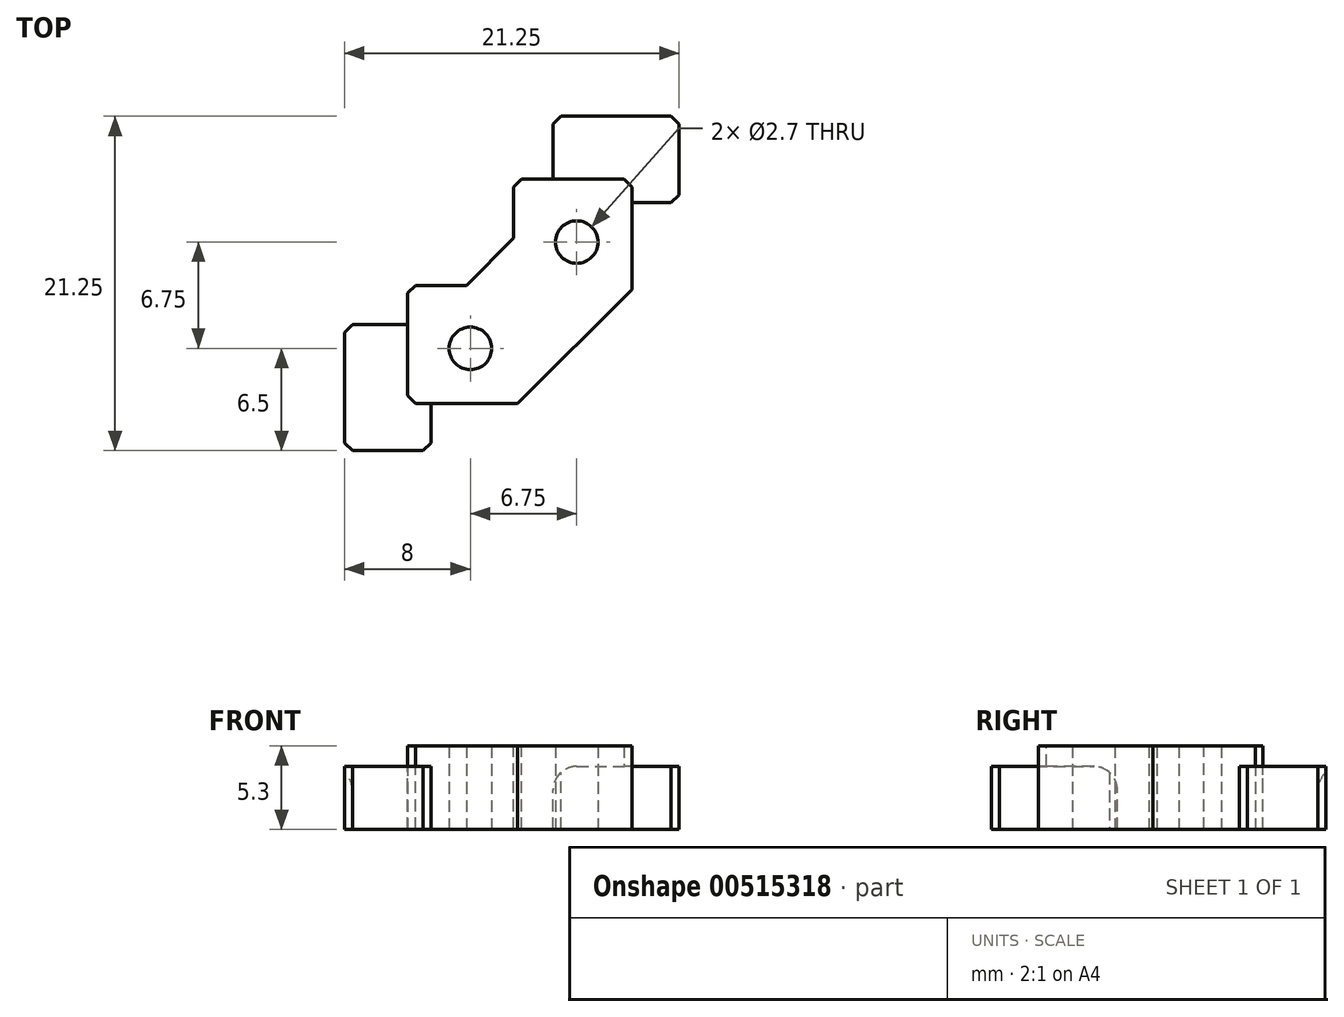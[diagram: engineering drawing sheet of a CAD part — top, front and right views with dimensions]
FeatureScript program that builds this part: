
annotation { "Feature Type Name" : "Feature", "Feature Type Description" : "" }
export const myFeature = defineFeature(function(context is Context, id is Id, definition is map)
    precondition{}
    {
        {
            var Q0;
            Q0=qCreatedBy(makeId("Top.planeOp"),FACE);
            var sketch = newSketch(context, id + "F0", { "sketchPlane" : qUnion([Q0])});
            skLineSegment(sketch, "E0", {"start": v(-0.25, -7) * mm, "end": v(7, 0.25) * mm});
            skLineSegment(sketch, "E1", {"start": v(7, 7.25) * mm, "end": v(7, 0.25) * mm});
            skLineSegment(sketch, "E2", {"start": v(-7.25, -7) * mm, "end": v(-0.25, -7) * mm});
            skLineSegment(sketch, "E3", {"start": v(-0.5, 7.25) * mm, "end": v(-0.5, 0.5) * mm});
            skLineSegment(sketch, "E4", {"start": v(-7.25, 0.5) * mm, "end": v(-0.5, 0.5) * mm});
            skLineSegment(sketch, "E5", {"start": v(-0.5, 7.25) * mm, "end": v(7, 7.25) * mm});
            skLineSegment(sketch, "E6", {"start": v(-7.25, 0.5) * mm, "end": v(-7.25, -7) * mm});
            skSolve(sketch);
        }
        {
            var Q0;
            Q0=qSketchRegion(id+"F0",true);
            extrude(context, id + "F1", {"entities" : qUnion([Q0]), "depth" : 1.3 * mm, "offsetDistance" : 25 * mm});
        }
        {
            var Q0;
            Q0=makeQuery(id+"F1.opExtrude","CAP_FACE",FACE,{"disambiguationData":[OSD([sQuery(id+"F0.wireOp",EDGE,"E0"),sQuery(id+"F0.wireOp",EDGE,"E1"),sQuery(id+"F0.wireOp",EDGE,"E2"),sQuery(id+"F0.wireOp",EDGE,"E3"),sQuery(id+"F0.wireOp",EDGE,"E4"),sQuery(id+"F0.wireOp",EDGE,"E5"),sQuery(id+"F0.wireOp",EDGE,"E6")])],"isStart":true});
            var sketch = newSketch(context, id + "F2", { "sketchPlane" : qUnion([Q0])});
            skLineSegment(sketch, "E7", {"start": v(7, -0.25) * mm, "end": v(-0.25, 7) * mm});
            skLineSegment(sketch, "E8", {"start": v(-11.25, 10) * mm, "end": v(-11.25, 2) * mm});
            skLineSegment(sketch, "E9", {"start": v(-11.25, 2) * mm, "end": v(-7.25, 2) * mm});
            skLineSegment(sketch, "E10", {"start": v(-7.25, 2) * mm, "end": v(-7.25, -0.5) * mm});
            skLineSegment(sketch, "E11", {"start": v(-7.25, -0.5) * mm, "end": v(-0.5, -0.5) * mm});
            skLineSegment(sketch, "E12", {"start": v(-0.5, -0.5) * mm, "end": v(-0.5, -7.25) * mm});
            skLineSegment(sketch, "E13", {"start": v(-0.5, -7.25) * mm, "end": v(2, -7.25) * mm});
            skLineSegment(sketch, "E14", {"start": v(2, -7.25) * mm, "end": v(2, -11.25) * mm});
            skLineSegment(sketch, "E15", {"start": v(2, -11.25) * mm, "end": v(10, -11.25) * mm});
            skLineSegment(sketch, "E16", {"start": v(-0.25, 7) * mm, "end": v(-5.75, 7) * mm});
            skLineSegment(sketch, "E17", {"start": v(-5.75, 7) * mm, "end": v(-5.75, 10) * mm});
            skLineSegment(sketch, "E18", {"start": v(-5.75, 10) * mm, "end": v(-11.25, 10) * mm});
            skLineSegment(sketch, "E19", {"start": v(7, -5.75) * mm, "end": v(10, -5.75) * mm});
            skLineSegment(sketch, "E20", {"start": v(10, -5.75) * mm, "end": v(10, -11.25) * mm});
            skLineSegment(sketch, "E21", {"start": v(7, -0.25) * mm, "end": v(7, -5.75) * mm});
            skSolve(sketch);
        }
        {
            var Q0;
            Q0=qSketchRegion(id+"F2",true);
            extrude(context, id + "F3", {"entities" : qUnion([Q0]), "operationType" : NewBodyOperationType.ADD, "depth" : 4 * mm, "offsetDistance" : 25 * mm});
        }
        {
            var Q0;
            Q0=makeQuery(id+"F3.opExtrude","SWEPT_EDGE",EDGE,{"disambiguationData":[OSD([sQuery(id+"F2.wireOp",EDGE,"E17"),sQuery(id+"F2.wireOp",EDGE,"E18")])]});
            var Q1;
            Q1=makeQuery(id+"F3.opExtrude","SWEPT_EDGE",EDGE,{"disambiguationData":[OSD([sQuery(id+"F2.wireOp",EDGE,"E8"),sQuery(id+"F2.wireOp",EDGE,"E18")])]});
            var Q2;
            Q2=makeQuery(id+"F1.opExtrude","SWEPT_EDGE",EDGE,{"disambiguationData":[OSD([sQuery(id+"F0.wireOp",EDGE,"E2"),sQuery(id+"F0.wireOp",EDGE,"E6")])]});
            var Q3;
            Q3=makeQuery(id+"F3.opExtrude","SWEPT_EDGE",EDGE,{"disambiguationData":[OSD([sQuery(id+"F2.wireOp",EDGE,"E8"),sQuery(id+"F2.wireOp",EDGE,"E9")])]});
            var Q4;
            Q4=makeQuery(id+"F3.boolean.opBoolean","MERGE",EDGE,{"derivedFrom":[makeQuery(id+"F1.opExtrude","SWEPT_EDGE",EDGE,{"disambiguationData":[OSD([sQuery(id+"F0.wireOp",EDGE,"E4"),sQuery(id+"F0.wireOp",EDGE,"E6")])]}),makeQuery(id+"F3.opExtrude","SWEPT_EDGE",EDGE,{"disambiguationData":[OSD([sQuery(id+"F2.wireOp",EDGE,"E10"),sQuery(id+"F2.wireOp",EDGE,"E11")])]})]});
            var Q5;
            Q5=makeQuery(id+"F3.boolean.opBoolean","MERGE",EDGE,{"derivedFrom":[makeQuery(id+"F1.opExtrude","SWEPT_EDGE",EDGE,{"disambiguationData":[OSD([sQuery(id+"F0.wireOp",EDGE,"E3"),sQuery(id+"F0.wireOp",EDGE,"E5")])]}),makeQuery(id+"F3.opExtrude","SWEPT_EDGE",EDGE,{"disambiguationData":[OSD([sQuery(id+"F2.wireOp",EDGE,"E12"),sQuery(id+"F2.wireOp",EDGE,"E13")])]})]});
            var Q6;
            Q6=makeQuery(id+"F3.opExtrude","SWEPT_EDGE",EDGE,{"disambiguationData":[OSD([sQuery(id+"F2.wireOp",EDGE,"E14"),sQuery(id+"F2.wireOp",EDGE,"E15")])]});
            var Q7;
            Q7=makeQuery(id+"F1.opExtrude","SWEPT_EDGE",EDGE,{"disambiguationData":[OSD([sQuery(id+"F0.wireOp",EDGE,"E1"),sQuery(id+"F0.wireOp",EDGE,"E5")])]});
            var Q8;
            Q8=makeQuery(id+"F3.opExtrude","SWEPT_EDGE",EDGE,{"disambiguationData":[OSD([sQuery(id+"F2.wireOp",EDGE,"E15"),sQuery(id+"F2.wireOp",EDGE,"E20")])]});
            var Q9;
            Q9=makeQuery(id+"F3.opExtrude","SWEPT_EDGE",EDGE,{"disambiguationData":[OSD([sQuery(id+"F2.wireOp",EDGE,"E19"),sQuery(id+"F2.wireOp",EDGE,"E20")])]});
            chamfer(context, id + "F4", {"entities" : qUnion([Q0, Q1, Q2, Q3, Q4, Q5, Q6, Q7, Q8, Q9]), "width" : .5 * mm, "tangentPropagation" : true});
        }
        {
            var Q0;
            Q0=makeQuery(id+"F3.boolean.opBoolean","MERGE",EDGE,{"derivedFrom":[makeQuery(id+"F1.opExtrude","SWEPT_EDGE",EDGE,{"disambiguationData":[OSD([sQuery(id+"F0.wireOp",EDGE,"E3"),sQuery(id+"F0.wireOp",EDGE,"E4")])]}),makeQuery(id+"F3.opExtrude","SWEPT_EDGE",EDGE,{"disambiguationData":[OSD([sQuery(id+"F2.wireOp",EDGE,"E11"),sQuery(id+"F2.wireOp",EDGE,"E12")])]})]});
            chamfer(context, id + "F5", {"entities" : qUnion([Q0]), "width" : 3 * mm, "tangentPropagation" : true});
        }
        {
            var Q0;
            Q0=makeQuery(id+"F3.opExtrude","CAP_EDGE",EDGE,{"disambiguationData":[OSD([sQuery(id+"F2.wireOp",EDGE,"E14")])],"isStart":true});
            var Q1;
            Q1=makeQuery(id+"F3.opExtrude","CAP_EDGE",EDGE,{"disambiguationData":[OSD([sQuery(id+"F2.wireOp",EDGE,"E9")])],"isStart":true});
            fillet(context, id + "F6", {"entities" : qUnion([Q0, Q1]), "radius" : 1.5 * mm, "tangentPropagation" : true, "allowEdgeOverflow" : false});
        }
        {
            var Q0;
            Q0=makeQuery(id+"F1.opExtrude","CAP_FACE",FACE,{"disambiguationData":[OSD([sQuery(id+"F0.wireOp",EDGE,"E0"),sQuery(id+"F0.wireOp",EDGE,"E1"),sQuery(id+"F0.wireOp",EDGE,"E2"),sQuery(id+"F0.wireOp",EDGE,"E3"),sQuery(id+"F0.wireOp",EDGE,"E4"),sQuery(id+"F0.wireOp",EDGE,"E5"),sQuery(id+"F0.wireOp",EDGE,"E6")])],"isStart":false});
            var sketch = newSketch(context, id + "F7", { "sketchPlane" : qUnion([Q0])});
            skPoint(sketch, "E22", {"position": v(3.5, 3.25) * mm});
            skPoint(sketch, "E23", {"position": v(-3.25, -3.5) * mm});
            skSolve(sketch);
        }
        {
            var Q0;
            Q0=sQuery(id+"F7.wireOp",VERTEX,"E22");
            var Q1;
            Q1=sQuery(id+"F7.wireOp",VERTEX,"E23");
            var Q2;
            Q2=makeQuery(id+"F1.opExtrude","SWEPT_BODY",BODY,{"disambiguationData":[OSD([sQuery(id+"F0.wireOp",EDGE,"E0"),sQuery(id+"F0.wireOp",EDGE,"E1"),sQuery(id+"F0.wireOp",EDGE,"E2"),sQuery(id+"F0.wireOp",EDGE,"E3"),sQuery(id+"F0.wireOp",EDGE,"E4"),sQuery(id+"F0.wireOp",EDGE,"E5"),sQuery(id+"F0.wireOp",EDGE,"E6")])]});
            hole(context, id + "F8", {"style" : HoleStyle.SIMPLE, "endStyle" : HoleEndStyle.THROUGH, "holeDiameter" : 2.7 * mm, "majorDiameter" : 5 * mm, "isTappedThrough" : true, "tappedDepth" : 12 * mm, "tapClearance" : 3, "locations" : qUnion([Q0, Q1]), "scope" : qUnion([Q2]), "startStyle" : HoleStartStyle.SKETCH});
        }
    });
